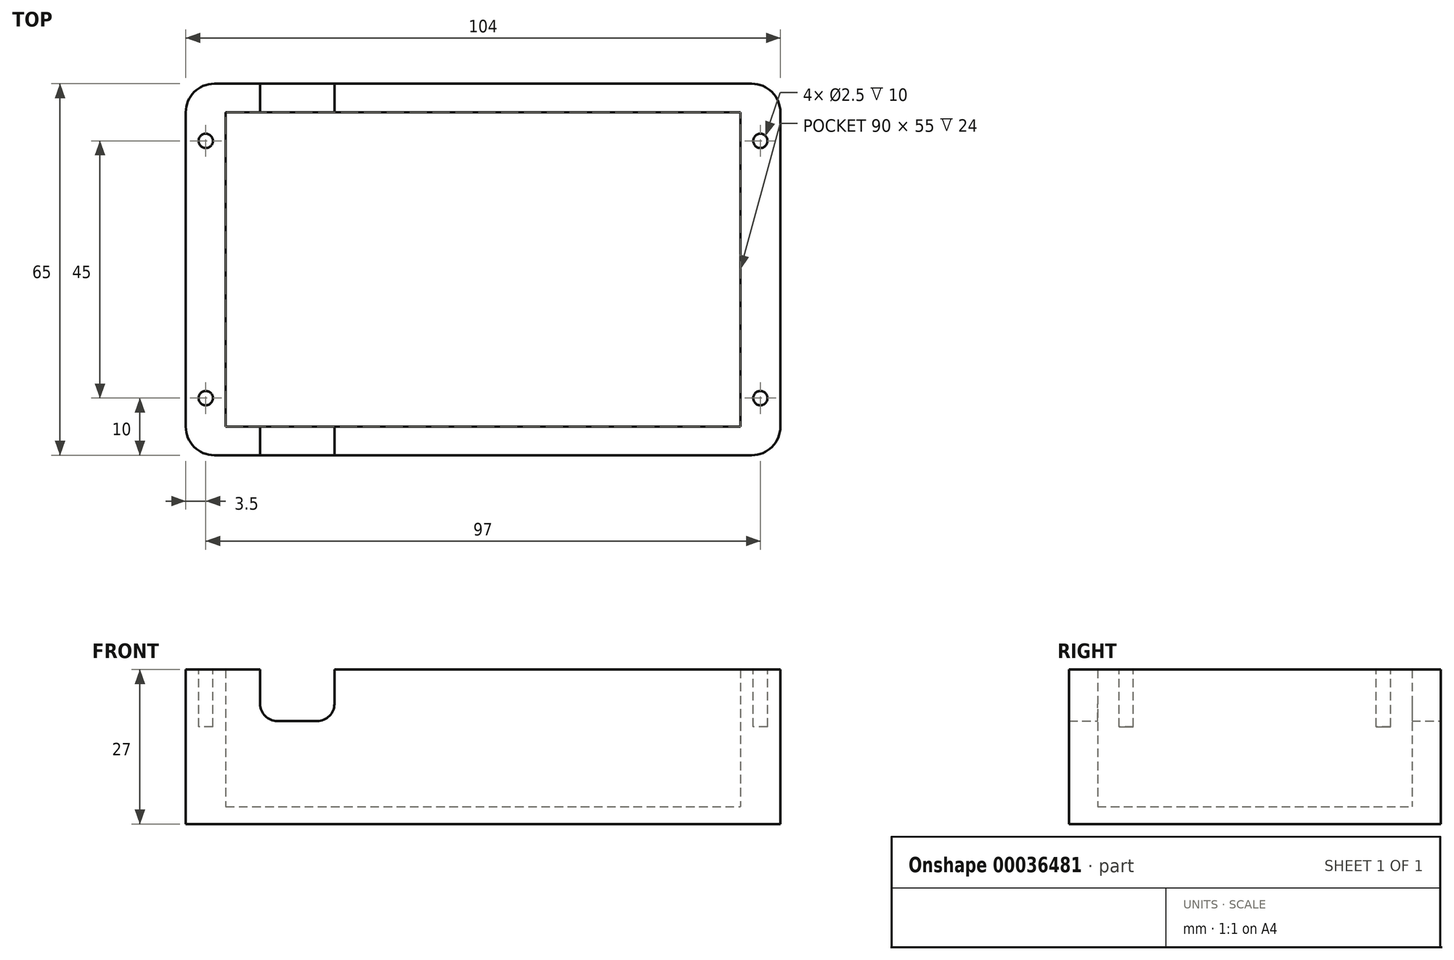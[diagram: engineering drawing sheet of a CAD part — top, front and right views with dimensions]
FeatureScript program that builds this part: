
annotation { "Feature Type Name" : "Feature", "Feature Type Description" : "" }
export const myFeature = defineFeature(function(context is Context, id is Id, definition is map)
    precondition{}
    {
        {
            var Q0;
            Q0=qCreatedBy(makeId("Top.planeOp"),FACE);
            var sketch = newSketch(context, id + "F0", { "sketchPlane" : qUnion([Q0])});
            skLineSegment(sketch, "E0.bottom", {"start": v(5, 0) * mm, "end": v(99, 0) * mm});
            skLineSegment(sketch, "E0.top", {"start": v(5, 65) * mm, "end": v(99, 65) * mm});
            skLineSegment(sketch, "E0.left", {"start": v(0, 5) * mm, "end": v(0, 60) * mm});
            skLineSegment(sketch, "E0.right", {"start": v(104, 5) * mm, "end": v(104, 60) * mm});
            skPoint(sketch, "E1.visualSharp", {"position": v(0, 65) * mm});
            skArc(sketch, "E1.filletArc", {"start": v(5, 65) * mm, "mid": v(1.46, 63.54) * mm, "end": v(0, 60) * mm});
            skPoint(sketch, "E2.visualSharp", {"position": v(104, 65) * mm});
            skArc(sketch, "E2.filletArc", {"start": v(104, 60) * mm, "mid": v(102.54, 63.54) * mm, "end": v(99, 65) * mm});
            skPoint(sketch, "E3.visualSharp", {"position": v(104, 0) * mm});
            skArc(sketch, "E3.filletArc", {"start": v(99, 0) * mm, "mid": v(102.54, 1.46) * mm, "end": v(104, 5) * mm});
            skPoint(sketch, "E4.visualSharp", {"position": v(0, 0) * mm});
            skArc(sketch, "E4.filletArc", {"start": v(0, 5) * mm, "mid": v(1.46, 1.46) * mm, "end": v(5, 0) * mm});
            skSolve(sketch);
        }
        {
            var Q0;
            Q0 = qSketchRegion(id + "F0", true);
            extrude(context, id + "F1", {"entities" : qUnion([Q0]), "depth" : 3 * mm});
        }
        {
            var Q0;
            Q0=makeQuery(id+"F1.opExtrude","CAP_FACE",FACE,{"disambiguationData":[OSD([sQuery(id+"F0.wireOp",EDGE,"E0.bottom"),sQuery(id+"F0.wireOp",EDGE,"E0.top"),sQuery(id+"F0.wireOp",EDGE,"E0.left"),sQuery(id+"F0.wireOp",EDGE,"E0.right")])],"isStart":false});
            var sketch = newSketch(context, id + "F2", { "sketchPlane" : qUnion([Q0])});
            skLineSegment(sketch, "E5.bottom", {"start": v(7, 5) * mm, "end": v(97, 5) * mm});
            skLineSegment(sketch, "E5.top", {"start": v(7, 60) * mm, "end": v(97, 60) * mm});
            skLineSegment(sketch, "E5.left", {"start": v(7, 5) * mm, "end": v(7, 60) * mm});
            skLineSegment(sketch, "E5.right", {"start": v(97, 5) * mm, "end": v(97, 60) * mm});
            skSolve(sketch);
        }
        {
            var Q0;
            Q0=makeQuery(id+"F2.imprint","IMPRINT",FACE,{"disambiguationData":[TD([[makeQuery(id+"F2.imprint","IMPRINT",EDGE,{"derivedFrom":sQuery(id+"F2.wireOp",EDGE,"E5.bottom")}),-1.0]])]});
            extrude(context, id + "F3", {"entities" : qUnion([Q0]), "operationType" : NewBodyOperationType.ADD, "depth" : 24 * mm});
        }
        {
            var Q0;
            Q0=makeQuery(id+"F3.opExtrude","CAP_FACE",FACE,{"disambiguationData":[OSD([sQuery(id+"F0.wireOp",EDGE,"E0.bottom"),sQuery(id+"F0.wireOp",EDGE,"E0.top"),sQuery(id+"F0.wireOp",EDGE,"E0.left"),sQuery(id+"F0.wireOp",EDGE,"E0.right"),sQuery(id+"F0.wireOp",EDGE,"E1.filletArc"),sQuery(id+"F0.wireOp",EDGE,"E2.filletArc"),sQuery(id+"F0.wireOp",EDGE,"E3.filletArc"),sQuery(id+"F0.wireOp",EDGE,"E4.filletArc"),sQuery(id+"F2.wireOp",EDGE,"E5.bottom"),sQuery(id+"F2.wireOp",EDGE,"E5.top"),sQuery(id+"F2.wireOp",EDGE,"E5.left"),sQuery(id+"F2.wireOp",EDGE,"E5.right")])],"isStart":false});
            var sketch = newSketch(context, id + "F4", { "sketchPlane" : qUnion([Q0])});
            skCircle(sketch, "E6", {"center": v(3.5, 10) * mm, "radius": 1.25 * mm});
            skCircle(sketch, "E7", {"center": v(100.5, 55) * mm, "radius": 1.25 * mm});
            skLineSegment(sketch, "E8", {"start": v(0, 32.5) * mm, "end": v(104, 32.5) * mm});
            skCircle(sketch, "E9.MirrorC", {"center": v(100.5, 10) * mm, "radius": 1.25 * mm});
            skCircle(sketch, "E10.MirrorC", {"center": v(3.5, 55) * mm, "radius": 1.25 * mm});
            skSolve(sketch);
        }
        {
            var Q0;
            Q0 = qSketchRegion(id + "F4", true);
            extrude(context, id + "F5", {"entities" : qUnion([Q0]), "operationType" : NewBodyOperationType.REMOVE, "oppositeDirection" : true, "depth" : 10 * mm});
        }
        {
            var Q0;
            Q0=makeQuery(id+"F3.opExtrude","CAP_FACE",FACE,{"disambiguationData":[OSD([sQuery(id+"F0.wireOp",EDGE,"E0.bottom"),sQuery(id+"F0.wireOp",EDGE,"E0.top"),sQuery(id+"F0.wireOp",EDGE,"E0.left"),sQuery(id+"F0.wireOp",EDGE,"E0.right"),sQuery(id+"F0.wireOp",EDGE,"E1.filletArc"),sQuery(id+"F0.wireOp",EDGE,"E2.filletArc"),sQuery(id+"F0.wireOp",EDGE,"E3.filletArc"),sQuery(id+"F0.wireOp",EDGE,"E4.filletArc"),sQuery(id+"F2.wireOp",EDGE,"E5.bottom"),sQuery(id+"F2.wireOp",EDGE,"E5.top"),sQuery(id+"F2.wireOp",EDGE,"E5.left"),sQuery(id+"F2.wireOp",EDGE,"E5.right")])],"isStart":false});
            var sketch = newSketch(context, id + "F6", { "sketchPlane" : qUnion([Q0])});
            skLineSegment(sketch, "E11.bottom", {"start": v(13, 0) * mm, "end": v(26, 0) * mm});
            skLineSegment(sketch, "E11.top", {"start": v(13, 65) * mm, "end": v(26, 65) * mm});
            skLineSegment(sketch, "E11.left", {"start": v(13, 0) * mm, "end": v(13, 65) * mm});
            skLineSegment(sketch, "E11.right", {"start": v(26, 0) * mm, "end": v(26, 65) * mm});
            skSolve(sketch);
        }
        {
            var Q0;
            Q0 = qSketchRegion(id + "F6", true);
            extrude(context, id + "F7", {"entities" : qUnion([Q0]), "operationType" : NewBodyOperationType.REMOVE, "oppositeDirection" : true, "depth" : 9 * mm});
        }
        {
            var Q0;
            Q0=makeQuery(id+"F7.boolean.opBoolean","COPY",EDGE,{"disambiguationData":[OD(0.0)],"derivedFrom":makeQuery(id+"F7.opExtrude","CAP_EDGE",EDGE,{"disambiguationData":[OSD([sQuery(id+"F6.wireOp",EDGE,"E11.right")])],"isStart":false})});
            var Q1;
            Q1=makeQuery(id+"F7.boolean.opBoolean","COPY",EDGE,{"disambiguationData":[OD(0.0)],"derivedFrom":makeQuery(id+"F7.opExtrude","CAP_EDGE",EDGE,{"disambiguationData":[OSD([sQuery(id+"F6.wireOp",EDGE,"E11.left")])],"isStart":false})});
            var Q2;
            Q2=makeQuery(id+"F7.boolean.opBoolean","COPY",EDGE,{"disambiguationData":[OD(1.0)],"derivedFrom":makeQuery(id+"F7.opExtrude","CAP_EDGE",EDGE,{"disambiguationData":[OSD([sQuery(id+"F6.wireOp",EDGE,"E11.left")])],"isStart":false})});
            var Q3;
            Q3=makeQuery(id+"F7.boolean.opBoolean","COPY",EDGE,{"disambiguationData":[OD(1.0)],"derivedFrom":makeQuery(id+"F7.opExtrude","CAP_EDGE",EDGE,{"disambiguationData":[OSD([sQuery(id+"F6.wireOp",EDGE,"E11.right")])],"isStart":false})});
            fillet(context, id + "F8", {"entities" : qUnion([Q0, Q1, Q2, Q3]), "radius" : 3 * mm, "tangentPropagation" : true, "allowEdgeOverflow" : false});
        }
    });
